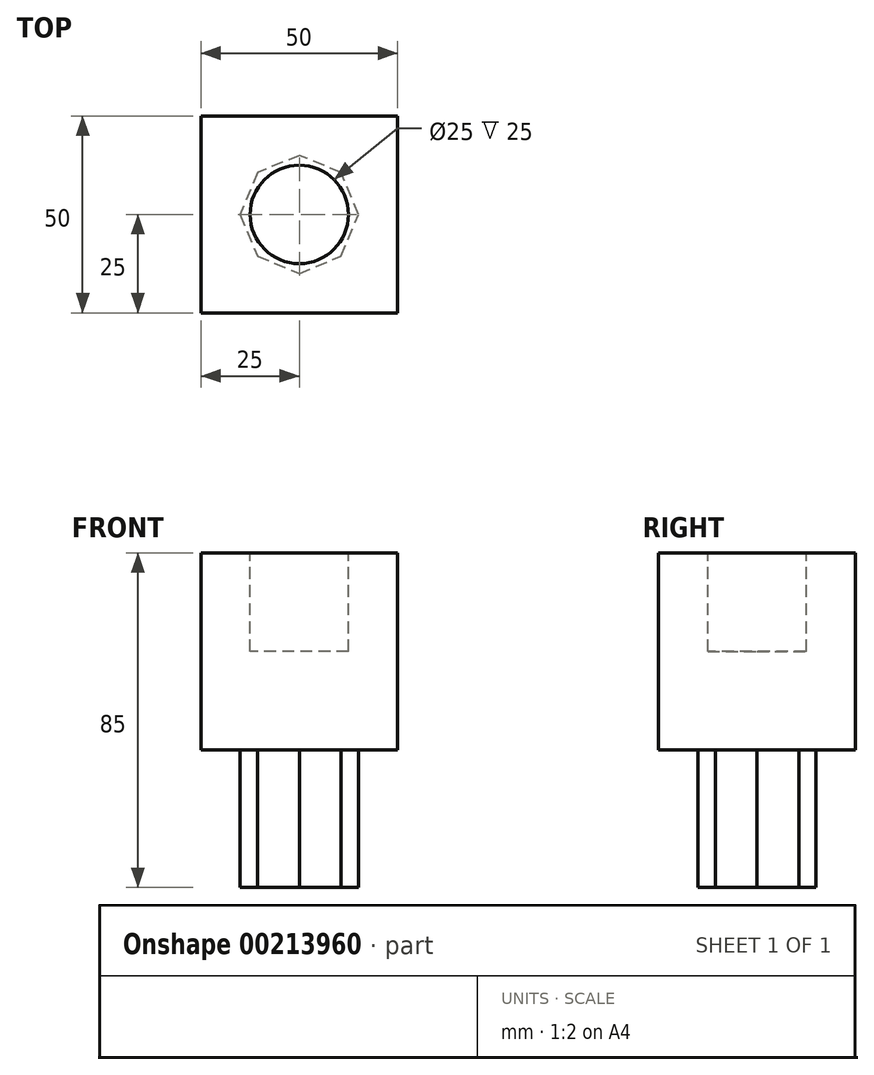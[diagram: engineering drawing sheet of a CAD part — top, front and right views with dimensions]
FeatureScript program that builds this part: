
annotation { "Feature Type Name" : "Feature", "Feature Type Description" : "" }
export const myFeature = defineFeature(function(context is Context, id is Id, definition is map)
    precondition{}
    {
        {
            var Q0;
            Q0=qCreatedBy(makeId("Top.planeOp"),FACE);
            var sketch = newSketch(context, id + "F0", { "sketchPlane" : qUnion([Q0])});
            skLineSegment(sketch, "E0.bottom", {"start": v(-25, 25) * mm, "end": v(25, 25) * mm});
            skLineSegment(sketch, "E0.top", {"start": v(-25, -25) * mm, "end": v(25, -25) * mm});
            skLineSegment(sketch, "E0.left", {"start": v(-25, 25) * mm, "end": v(-25, -25) * mm});
            skLineSegment(sketch, "E0.right", {"start": v(25, 25) * mm, "end": v(25, -25) * mm});
            skSolve(sketch);
        }
        {
            var Q0;
            Q0 = qSketchRegion(id + "F0", true);
            extrude(context, id + "F1", {"entities" : qUnion([Q0]), "depth" : 50 * mm});
        }
        {
            var Q0;
            Q0=makeQuery(id+"F1.opExtrude","CAP_FACE",FACE,{"disambiguationData":[OSD([sQuery(id+"F0.wireOp",EDGE,"E0.bottom"),sQuery(id+"F0.wireOp",EDGE,"E0.top"),sQuery(id+"F0.wireOp",EDGE,"E0.left"),sQuery(id+"F0.wireOp",EDGE,"E0.right")])],"isStart":false});
            var sketch = newSketch(context, id + "F2", { "sketchPlane" : qUnion([Q0])});
            skCircle(sketch, "E1", {"center": v(0, 0) * mm, "radius": 12.5 * mm});
            skSolve(sketch);
        }
        {
            var Q0;
            Q0 = qSketchRegion(id + "F2", true);
            extrude(context, id + "F3", {"entities" : qUnion([Q0]), "operationType" : NewBodyOperationType.REMOVE, "oppositeDirection" : true, "depth" : 25 * mm});
        }
        {
            var Q0;
            Q0=makeQuery(id+"F1.opExtrude","CAP_FACE",FACE,{"disambiguationData":[OSD([sQuery(id+"F0.wireOp",EDGE,"E0.bottom"),sQuery(id+"F0.wireOp",EDGE,"E0.top"),sQuery(id+"F0.wireOp",EDGE,"E0.left"),sQuery(id+"F0.wireOp",EDGE,"E0.right")])],"isStart":true});
            var sketch = newSketch(context, id + "F4", { "sketchPlane" : qUnion([Q0])});
            skCircle(sketch, "E2.cCircle", {"center": v(0, 0) * mm, "radius": 15 * mm, "construction": true});
            skLineSegment(sketch, "E2.0", {"start": v(-10.6, 10.6) * mm, "end": v(0, 15) * mm});
            skLineSegment(sketch, "E2.1", {"start": v(0, 15) * mm, "end": v(10.6, 10.6) * mm});
            skLineSegment(sketch, "E2.2", {"start": v(10.6, 10.6) * mm, "end": v(15, 0) * mm});
            skLineSegment(sketch, "E2.3", {"start": v(15, 0) * mm, "end": v(10.6, -10.6) * mm});
            skLineSegment(sketch, "E2.4", {"start": v(10.6, -10.6) * mm, "end": v(0, -15) * mm});
            skLineSegment(sketch, "E2.5", {"start": v(0, -15) * mm, "end": v(-10.6, -10.6) * mm});
            skLineSegment(sketch, "E2.6", {"start": v(-10.6, -10.6) * mm, "end": v(-15, 0) * mm});
            skLineSegment(sketch, "E2.7", {"start": v(-15, 0) * mm, "end": v(-10.6, 10.6) * mm});
            skSolve(sketch);
        }
        {
            var Q0;
            Q0 = qSketchRegion(id + "F4", true);
            extrude(context, id + "F5", {"entities" : qUnion([Q0]), "operationType" : NewBodyOperationType.ADD, "depth" : 35 * mm});
        }
    });
